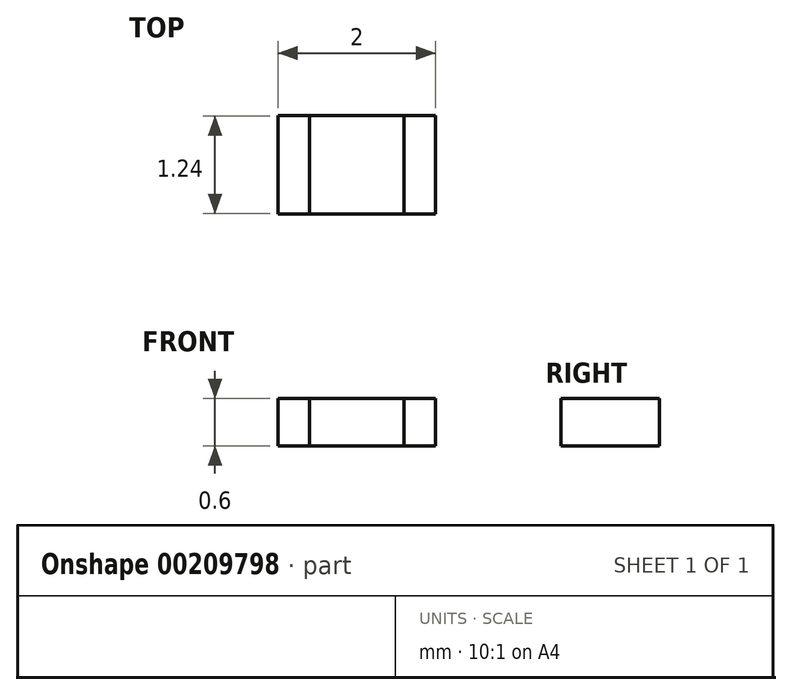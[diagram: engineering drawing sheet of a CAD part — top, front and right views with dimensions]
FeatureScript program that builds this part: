
annotation { "Feature Type Name" : "Feature", "Feature Type Description" : "" }
export const myFeature = defineFeature(function(context is Context, id is Id, definition is map)
    precondition{}
    {
        {
            var Q0;
            Q0=qCreatedBy(makeId("Top.planeOp"),FACE);
            var sketch = newSketch(context, id + "F0", { "sketchPlane" : qUnion([Q0]) });
            skLineSegment(sketch, "E0.bottom", {"start": v(-1, 0.63) * mm, "end": v(1, 0.63) * mm});
            skLineSegment(sketch, "E0.top", {"start": v(-1, -0.63) * mm, "end": v(1, -0.63) * mm});
            skLineSegment(sketch, "E0.left", {"start": v(-1, 0.63) * mm, "end": v(-1, -0.63) * mm});
            skLineSegment(sketch, "E0.right", {"start": v(1, 0.63) * mm, "end": v(1, -0.63) * mm});
            skLineSegment(sketch, "E1", {"start": v(-1, 0) * mm, "end": v(1, 0) * mm, "construction": true});
            skLineSegment(sketch, "E2", {"start": v(-0.6, 0.63) * mm, "end": v(-0.6, -0.63) * mm});
            skLineSegment(sketch, "E3.MirrorCS", {"start": v(0.6, 0.63) * mm, "end": v(0.6, -0.63) * mm});
            skSolve(sketch);
        }
        {
            var Q0;
            {var subQ0=sQuery(id+"F0.wireOp",EDGE,"E2");Q0=makeQuery(id+"F0.imprint","IMPRINT",FACE,{"disambiguationData":[TD([[makeQuery(id+"F0.imprint","IMPRINT",EDGE,{"derivedFrom":subQ0}),1.0]])]});}
            extrude(context, id + "F1", {"entities" : qUnion([Q0]), "depth" : 0.6 * mm});
        }
        {
            var Q0;
            {var subQ0=sQuery(id+"F0.wireOp",EDGE,"E0.left");Q0=makeQuery(id+"F0.imprint","IMPRINT",FACE,{"disambiguationData":[TD([[makeQuery(id+"F0.imprint","IMPRINT",EDGE,{"derivedFrom":subQ0}),1.0]])]});}
            var Q1;
            {var subQ0=sQuery(id+"F0.wireOp",EDGE,"E0.right");Q1=makeQuery(id+"F0.imprint","IMPRINT",FACE,{"disambiguationData":[TD([[makeQuery(id+"F0.imprint","IMPRINT",EDGE,{"derivedFrom":subQ0}),-1.0]])]});}
            var Q2;
            Q2=makeQuery(id+"F1.opExtrude","CAP_FACE",FACE,{"disambiguationData":[OSD([sQuery(id+"F0.wireOp",EDGE,"E0.bottom"),sQuery(id+"F0.wireOp",EDGE,"E0.top"),sQuery(id+"F0.wireOp",EDGE,"E2"),sQuery(id+"F0.wireOp",EDGE,"E3.MirrorCS")])],"isStart":false});
            extrude(context, id + "F2", {"entities" : qUnion([Q0, Q1]), "endBound" : BoundingType.UP_TO_SURFACE, "endBoundEntityFace" : qUnion([Q2]), "depth" : 25 * mm});
        }
    });
